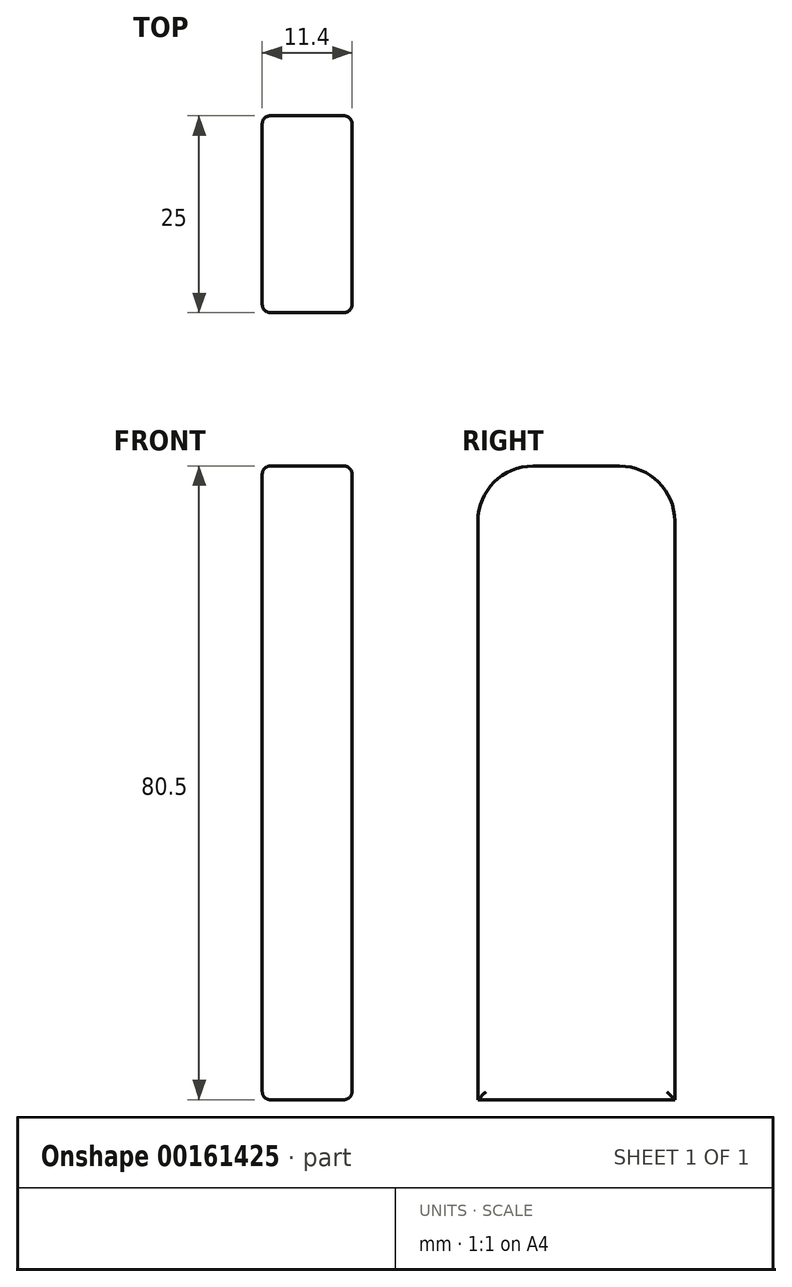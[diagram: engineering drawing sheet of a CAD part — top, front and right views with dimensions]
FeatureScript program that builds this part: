
annotation { "Feature Type Name" : "Feature", "Feature Type Description" : "" }
export const myFeature = defineFeature(function(context is Context, id is Id, definition is map)
    precondition{}
    {
        {
            var Q0;
            Q0=qCreatedBy(makeId("Front.planeOp"),FACE);
            var sketch = newSketch(context, id + "F0", { "sketchPlane" : qUnion([Q0])});
            skLineSegment(sketch, "E0.bottom", {"start": v(-3.7, 9) * mm, "end": v(3.7, 9) * mm});
            skLineSegment(sketch, "E0.left", {"start": v(-5.7, 9) * mm, "end": v(-5.7, 21.65) * mm});
            skLineSegment(sketch, "E1.left", {"start": v(-5.7, 11.32) * mm, "end": v(-5.7, 87.5) * mm});
            skLineSegment(sketch, "E1.right", {"start": v(5.7, 11.32) * mm, "end": v(5.7, 87.5) * mm});
            skPoint(sketch, "E1.middle", {"position": v(0, 54) * mm});
            skPoint(sketch, "E2.center.orphan", {"position": v(0, 42) * mm});
            skPoint(sketch, "E3.center.orphan", {"position": v(0, 30) * mm});
            skPoint(sketch, "E4.center.orphan", {"position": v(0, 66) * mm});
            skLineSegment(sketch, "E5", {"start": v(-3.7, 89.5) * mm, "end": v(3.3, 89.5) * mm});
            skPoint(sketch, "E6.center.orphan", {"position": v(0, 78) * mm});
            skPoint(sketch, "E7.orphan", {"position": v(-5.7, 96.68) * mm});
            skPoint(sketch, "E8.orphan", {"position": v(5.7, 96.68) * mm});
            skPoint(sketch, "E9.visualSharp", {"position": v(5.7, 89.5) * mm});
            skPoint(sketch, "E10.visualSharp", {"position": v(-5.7, 89.5) * mm});
            skLineSegment(sketch, "E11", {"start": v(5.7, 89.5) * mm, "end": v(5.7, 87.5) * mm});
            skLineSegment(sketch, "E12", {"start": v(5.7, 89.5) * mm, "end": v(3.3, 89.5) * mm});
            skLineSegment(sketch, "E13", {"start": v(-3.7, 89.5) * mm, "end": v(-5.7, 89.5) * mm});
            skLineSegment(sketch, "E14", {"start": v(-5.7, 89.5) * mm, "end": v(-5.7, 87.5) * mm});
            skLineSegment(sketch, "E15.top", {"start": v(5.7, 9) * mm, "end": v(3.7, 9) * mm});
            skLineSegment(sketch, "E15.left", {"start": v(5.7, 11.32) * mm, "end": v(5.7, 9) * mm});
            skLineSegment(sketch, "E16", {"start": v(-3.7, 9) * mm, "end": v(-5.7, 9) * mm});
            skSolve(sketch);
        }
        {
            var Q0;
            Q0=qSketchRegion(id+"F0",true);
            extrude(context, id + "F1", {"entities" : qUnion([Q0]), "depth" : 25 * mm});
        }
        {
            var Q0;
            Q0=makeQuery(id+"F1.opExtrude","SWEPT_FACE",FACE,{"disambiguationData":[OSD([sQuery(id+"F0.wireOp",EDGE,"E0.left"),sQuery(id+"F0.wireOp",EDGE,"E1.left"),sQuery(id+"F0.wireOp",EDGE,"E14")])]});
            var Q1;
            Q1=makeQuery(id+"FXsqYdtTdnNetYD_1.boolean.opBoolean","COPY",FACE,{"derivedFrom":makeQuery(id+"FXsqYdtTdnNetYD_1.opExtrude","SWEPT_FACE",FACE,{"disambiguationData":[OSD([sQuery(id+"FIX9SyF7r49jjJ3_1.wireOp",EDGE,"EXIJ8xsh-YSFm-b1v2-6XdE-JmGWGsUir2ZK")])]})});
            var Q2;
            Q2=makeQuery(id+"F1.opExtrude","SWEPT_FACE",FACE,{"disambiguationData":[OSD([sQuery(id+"F0.wireOp",EDGE,"E0.right"),sQuery(id+"F0.wireOp",EDGE,"E1.right"),sQuery(id+"F0.wireOp",EDGE,"E11")])]});
            var Q3;
            Q3=makeQuery(id+"FXsqYdtTdnNetYD_1.boolean.opBoolean","COPY",FACE,{"derivedFrom":makeQuery(id+"FXsqYdtTdnNetYD_1.opExtrude","SWEPT_FACE",FACE,{"disambiguationData":[OSD([sQuery(id+"FIX9SyF7r49jjJ3_1.wireOp",EDGE,"U2ydWebi-PYa6-6NHI-YzIc-XL9s0RwaVJjs")])]})});
            fillet(context, id + "F2", {"entities" : qUnion([Q0, Q1, Q2, Q3]), "radius" : 1 * mm, "tangentPropagation" : true, "allowEdgeOverflow" : false});
        }
        {
            var Q0;
            Q0=makeQuery(id+"F1.opExtrude","CAP_EDGE",EDGE,{"disambiguationData":[OSD([sQuery(id+"F0.wireOp",EDGE,"E5"),sQuery(id+"F0.wireOp",EDGE,"E12"),sQuery(id+"F0.wireOp",EDGE,"E13")])],"isStart":false});
            var Q1;
            Q1=makeQuery(id+"F1.opExtrude","CAP_EDGE",EDGE,{"disambiguationData":[OSD([sQuery(id+"F0.wireOp",EDGE,"E5"),sQuery(id+"F0.wireOp",EDGE,"E12"),sQuery(id+"F0.wireOp",EDGE,"E13")])],"isStart":true});
            fillet(context, id + "F3", {"entities" : qUnion([Q0, Q1]), "radius" : 7 * mm, "tangentPropagation" : true, "allowEdgeOverflow" : false});
        }
    });
